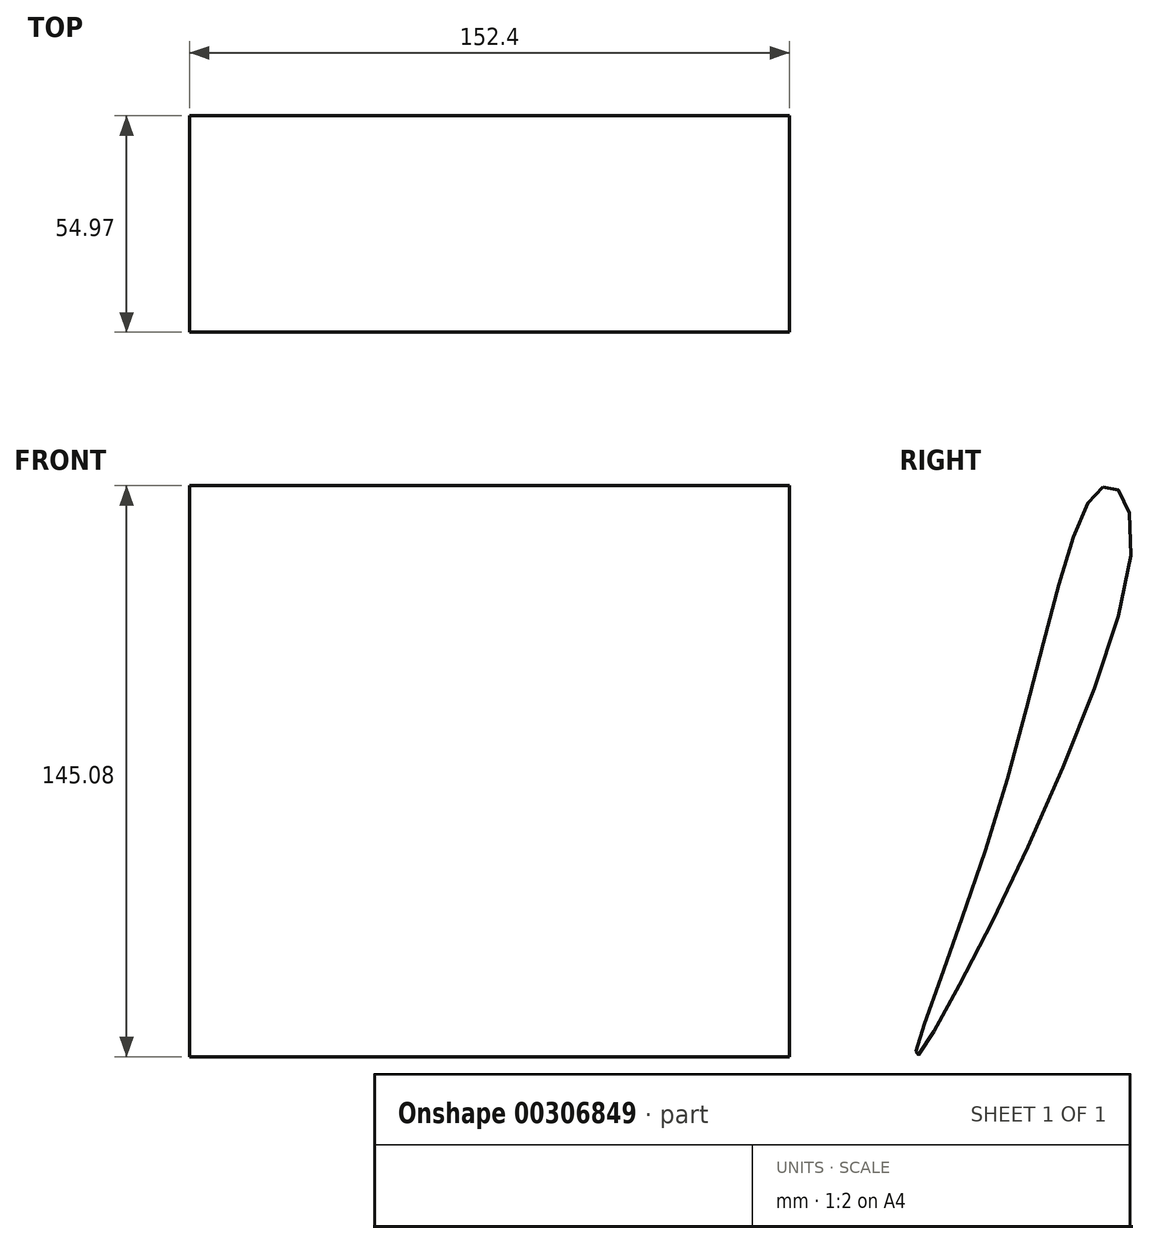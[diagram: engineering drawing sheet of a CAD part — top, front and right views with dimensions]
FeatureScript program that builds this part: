
annotation { "Feature Type Name" : "Feature", "Feature Type Description" : "" }
export const myFeature = defineFeature(function(context is Context, id is Id, definition is map)
    precondition{}
    {
        {
            var Q0;
            Q0=qCreatedBy(makeId("Right.planeOp"),FACE);
            var sketch = newSketch(context, id + "F0", { "sketchPlane" : qUnion([Q0])});
            skFitSpline(sketch, "E0", {"points": [v(44.88, 67.9) * mm, v(52.06, 51.86) * mm, v(-2.03, -76.46) * mm, v(18.89, -12.08) * mm, v(44.88, 67.9) * mm]});
            skSolve(sketch);
        }
        {
            var Q0;
            Q0=makeQuery(id+"F0.imprint","IMPRINT",FACE,{"disambiguationData":[TD([[makeQuery(id+"F0.imprint","IMPRINT",EDGE,{"derivedFrom":sQuery(id+"F0.wireOp",EDGE,"E0")}),-1.0]])]});
            extrude(context, id + "F1", {"entities" : qUnion([Q0]), "depth" : 76.2 * mm, "hasSecondDirection" : true, "secondDirectionOppositeDirection" : true, "secondDirectionDepth" : 76.2 * mm});
        }
    });
